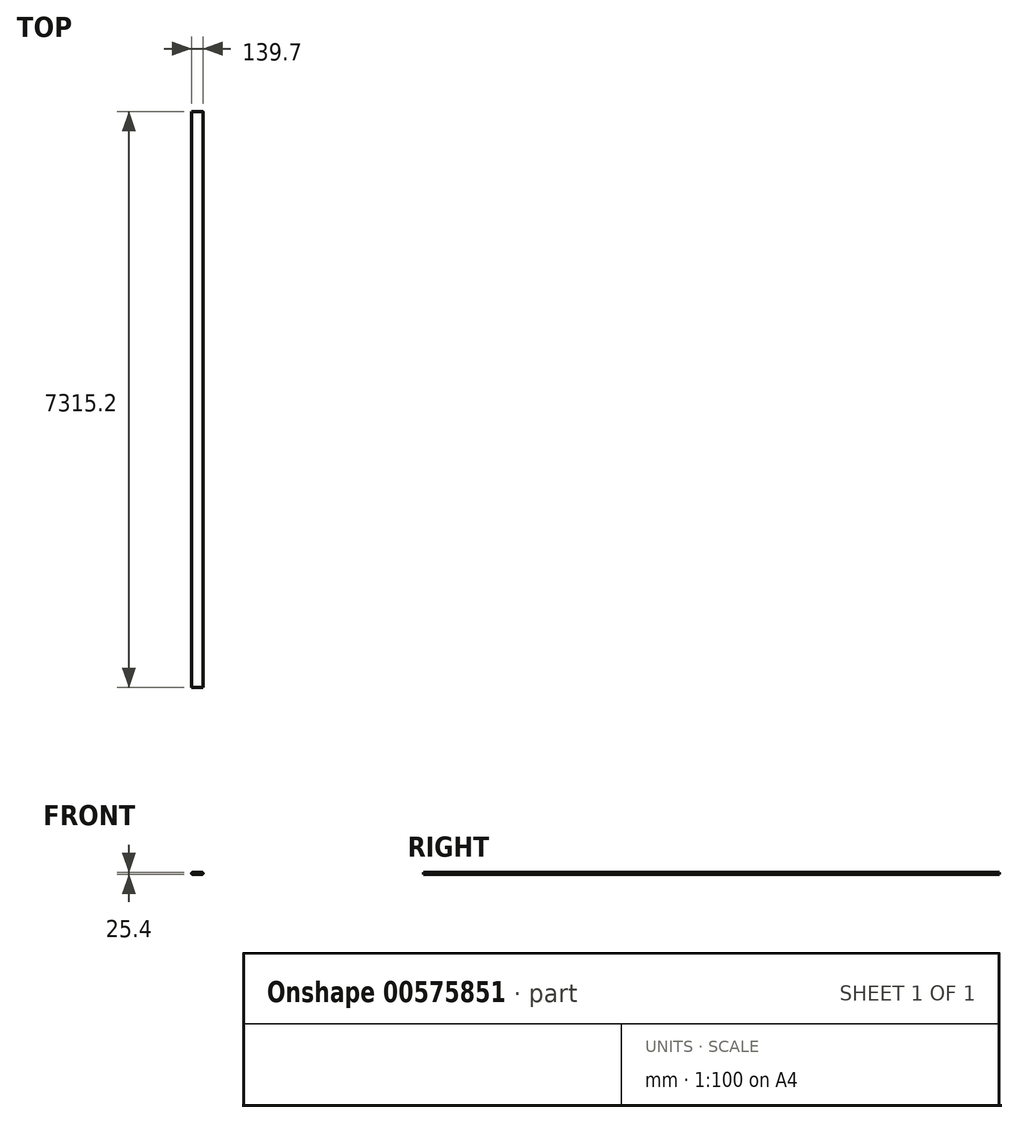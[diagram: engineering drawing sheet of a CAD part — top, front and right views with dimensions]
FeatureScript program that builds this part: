
annotation { "Feature Type Name" : "Feature", "Feature Type Description" : "" }
export const myFeature = defineFeature(function(context is Context, id is Id, definition is map)
    precondition{}
    {
        {
            var Q0;
            Q0=qCreatedBy(makeId("Front.planeOp"),FACE);
            var sketch = newSketch(context, id + "F0", { "sketchPlane" : qUnion([Q0])});
            skLineSegment(sketch, "E0.bottom", {"start": v(6.35, 0) * mm, "end": v(133.35, 0) * mm});
            skLineSegment(sketch, "E0.top", {"start": v(6.35, 25.4) * mm, "end": v(133.35, 25.4) * mm});
            skLineSegment(sketch, "E0.left", {"start": v(0, 6.35) * mm, "end": v(0, 19.05) * mm});
            skLineSegment(sketch, "E0.right", {"start": v(139.7, 6.35) * mm, "end": v(139.7, 19.05) * mm});
            skPoint(sketch, "E1.visualSharp", {"position": v(0, 25.4) * mm});
            skArc(sketch, "E1.filletArc", {"start": v(6.35, 25.4) * mm, "mid": v(1.86, 23.54) * mm, "end": v(0, 19.05) * mm});
            skPoint(sketch, "E2.visualSharp", {"position": v(139.7, 25.4) * mm});
            skArc(sketch, "E2.filletArc", {"start": v(139.7, 19.05) * mm, "mid": v(137.84, 23.54) * mm, "end": v(133.35, 25.4) * mm});
            skPoint(sketch, "E3.visualSharp", {"position": v(139.7, 0) * mm});
            skArc(sketch, "E3.filletArc", {"start": v(133.35, 0) * mm, "mid": v(137.84, 1.86) * mm, "end": v(139.7, 6.35) * mm});
            skPoint(sketch, "E4.visualSharp", {"position": v(0, 0) * mm});
            skArc(sketch, "E4.filletArc", {"start": v(0, 6.35) * mm, "mid": v(1.86, 1.86) * mm, "end": v(6.35, 0) * mm});
            skSolve(sketch);
        }
        {
            var Q0;
            Q0 = qSketchRegion(id + "F0", true);
            extrude(context, id + "F1", {"entities" : qUnion([Q0]), "depth" : 7315.2 * mm, "offsetDistance" : 25.4 * mm});
        }
    });
